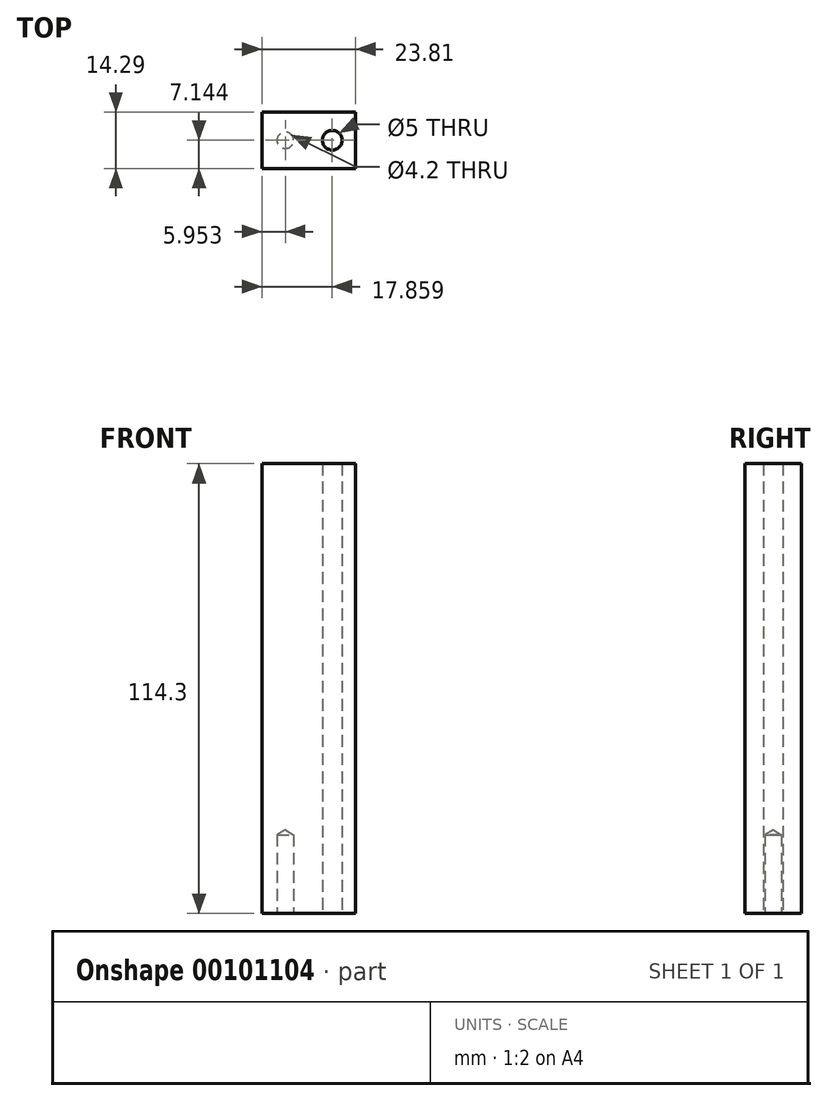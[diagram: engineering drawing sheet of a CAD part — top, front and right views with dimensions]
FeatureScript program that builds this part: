
annotation { "Feature Type Name" : "Feature", "Feature Type Description" : "" }
export const myFeature = defineFeature(function(context is Context, id is Id, definition is map)
    precondition{}
    {
        {
            var Q0;
            Q0=qCreatedBy(makeId("Top.planeOp"),FACE);
            var sketch = newSketch(context, id + "F0", { "sketchPlane" : qUnion([Q0])});
            skLineSegment(sketch, "E0.bottom", {"start": v(11.9, 14.29) * mm, "end": v(0, 14.29) * mm});
            skLineSegment(sketch, "E0.top", {"start": v(11.9, 0) * mm, "end": v(0, 0) * mm});
            skLineSegment(sketch, "E0.left", {"start": v(11.9, 14.29) * mm, "end": v(11.9, 0) * mm, "construction": true});
            skLineSegment(sketch, "E0.right", {"start": v(0, 14.29) * mm, "end": v(0, 0) * mm});
            skLineSegment(sketch, "E1.MirrorCS", {"start": v(23.81, 14.29) * mm, "end": v(23.81, 0) * mm});
            skLineSegment(sketch, "E2.MirrorCS", {"start": v(11.9, 0) * mm, "end": v(23.81, 0) * mm});
            skLineSegment(sketch, "E3.MirrorCS", {"start": v(11.9, 14.29) * mm, "end": v(23.81, 14.29) * mm});
            skCircle(sketch, "E4", {"center": v(5.95, 7.14) * mm, "radius": 2.5 * mm});
            skPoint(sketch, "E4.centerSnap0", {"position": v(0, 7.14) * mm});
            skPoint(sketch, "E4.centerSnap1", {"position": v(5.95, 14.29) * mm});
            skCircle(sketch, "E5.MirrorC", {"center": v(17.86, 7.14) * mm, "radius": 2.5 * mm});
            skSolve(sketch);
        }
        {
            var Q0;
            Q0=makeQuery(id+"F0.imprint","IMPRINT",FACE,{"disambiguationData":[TD([[makeQuery(id+"F0.imprint","IMPRINT",EDGE,{"derivedFrom":sQuery(id+"F0.wireOp",EDGE,"E0.bottom")}),1.0]])]});
            var Q1;
            Q1=makeQuery(id+"F0.imprint","IMPRINT",FACE,{"disambiguationData":[TD([[makeQuery(id+"F0.imprint","IMPRINT",EDGE,{"derivedFrom":sQuery(id+"F0.wireOp",EDGE,"E4")}),1.0]])]});
            var Q2;
            Q2=makeQuery(id+"F0.imprint","IMPRINT",FACE,{"disambiguationData":[TD([[makeQuery(id+"F0.imprint","IMPRINT",EDGE,{"derivedFrom":sQuery(id+"F0.wireOp",EDGE,"E5.MirrorC")}),-1.0]])]});
            extrude(context, id + "F1", {"entities" : qUnion([Q0, Q1, Q2]), "depth" : 114.3 * mm});
        }
        {
            var Q0;
            Q0=sQuery(id+"F0.wireOp",VERTEX,"E5.MirrorC.center");
            var Q1;
            Q1=sQuery(id+"F0.wireOp",VERTEX,"E4.center");
            var Q2;
            Q2=makeQuery(id+"F1.opExtrude","SWEPT_BODY",BODY,{"disambiguationData":[OSD([sQuery(id+"F0.wireOp",EDGE,"E0.bottom"),sQuery(id+"F0.wireOp",EDGE,"E0.top"),sQuery(id+"F0.wireOp",EDGE,"E0.right"),sQuery(id+"F0.wireOp",EDGE,"E1.MirrorCS"),sQuery(id+"F0.wireOp",EDGE,"E2.MirrorCS"),sQuery(id+"F0.wireOp",EDGE,"E3.MirrorCS")])]});
            hole(context, id + "F2", {"style" : HoleStyle.SIMPLE, "endStyle" : HoleEndStyle.BLIND, "oppositeDirection" : true, "standardTappedOrClearance" : lookupTablePath({ "standard" : "ISO", "engagement" : "75%", "pitch" : "0.8 mm", "size" : "M5", "type" : "Tapped" }), "standardBlindInLast" : lookupTablePath({ "standard" : "ISO", "engagement" : "75%", "pitch" : "0.8 mm", "size" : "M5", "type" : "Tapped" }), "holeDiameter" : 4.2 * mm, "holeDepth" : 20 * mm, "locations" : qUnion([Q0, Q1]), "scope" : qUnion([Q2]), "majorDiameter" : 5 * mm});
        }
    });
